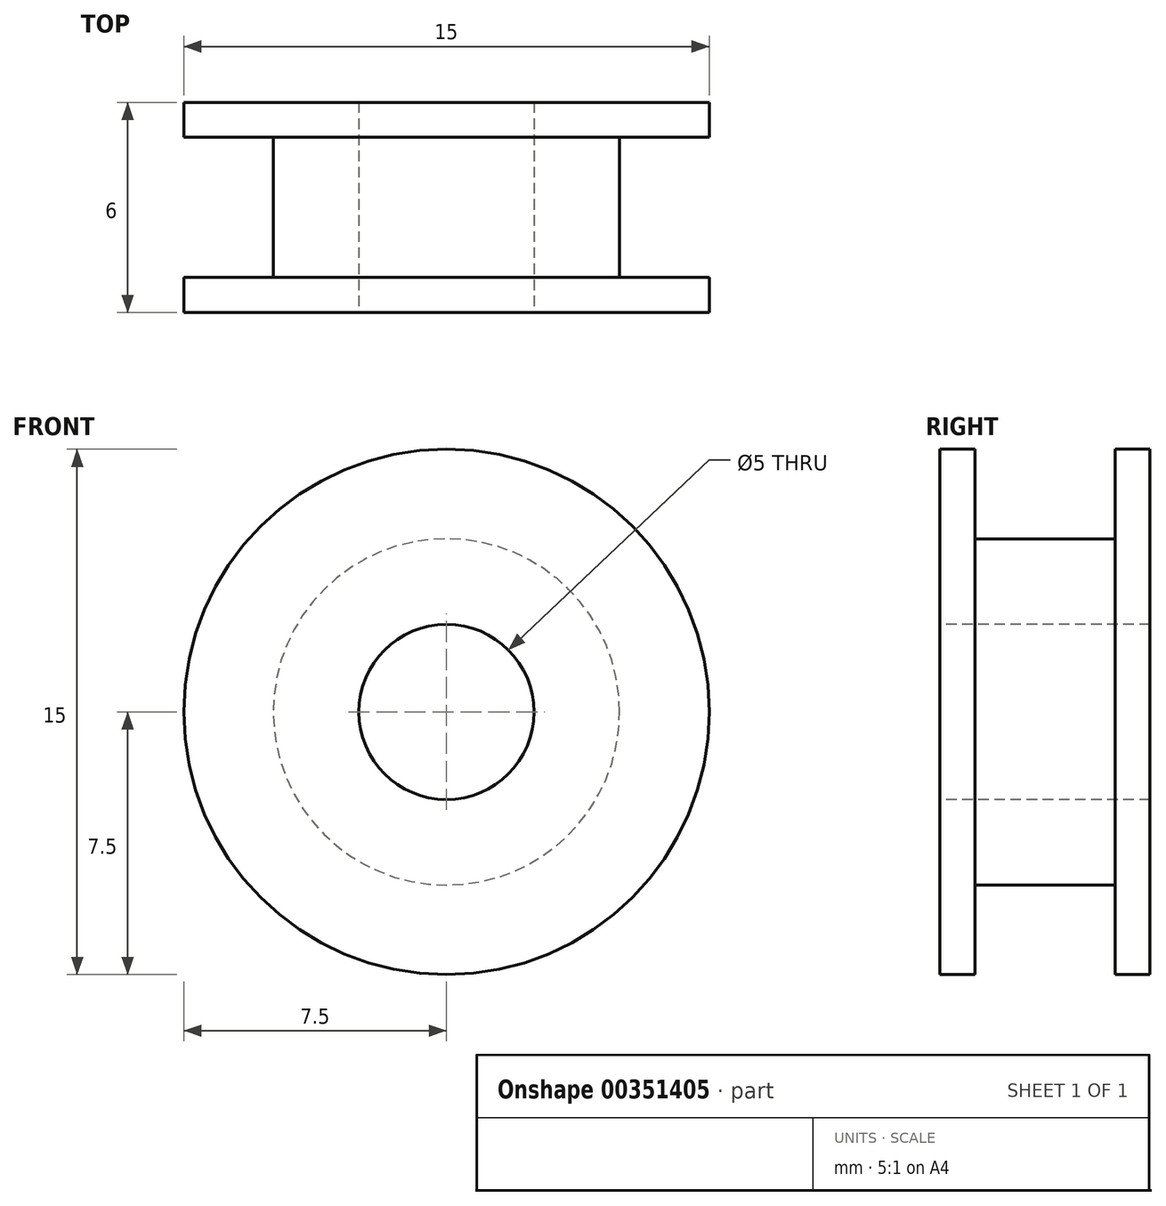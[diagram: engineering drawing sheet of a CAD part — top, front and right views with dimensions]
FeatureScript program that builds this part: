
annotation { "Feature Type Name" : "Feature", "Feature Type Description" : "" }
export const myFeature = defineFeature(function(context is Context, id is Id, definition is map)
    precondition{}
    {
        {
            var Q0;
            Q0=qCreatedBy(makeId("Front.planeOp"),FACE);
            var sketch = newSketch(context, id + "F0", { "sketchPlane" : qUnion([Q0])});
            skCircle(sketch, "E0", {"center": v(0, 0) * mm, "radius": 7.5 * mm});
            skSolve(sketch);
        }
        {
            var Q0;
            Q0 = qSketchRegion(id + "F0", true);
            extrude(context, id + "F1", {"entities" : qUnion([Q0]), "depth" : 1 * mm});
        }
        {
            var Q0;
            Q0=makeQuery(id+"F1.opExtrude","CAP_FACE",FACE,{"disambiguationData":[OSD([sQuery(id+"F0.wireOp",EDGE,"E0")])],"isStart":false});
            var sketch = newSketch(context, id + "F2", { "sketchPlane" : qUnion([Q0])});
            skCircle(sketch, "E1", {"center": v(0, 0) * mm, "radius": 4.94 * mm});
            skSolve(sketch);
        }
        {
            var Q0;
            Q0 = qSketchRegion(id + "F2", true);
            extrude(context, id + "F3", {"entities" : qUnion([Q0]), "operationType" : NewBodyOperationType.ADD, "depth" : 4 * mm});
        }
        {
            var Q0;
            Q0=makeQuery(id+"F3.opExtrude","CAP_FACE",FACE,{"disambiguationData":[OSD([sQuery(id+"F2.wireOp",EDGE,"E1")])],"isStart":false});
            var sketch = newSketch(context, id + "F4", { "sketchPlane" : qUnion([Q0])});
            skCircle(sketch, "E2", {"center": v(0, 0) * mm, "radius": 7.5 * mm});
            skSolve(sketch);
        }
        {
            var Q0;
            Q0 = qSketchRegion(id + "F4", true);
            extrude(context, id + "F5", {"entities" : qUnion([Q0]), "operationType" : NewBodyOperationType.ADD, "depth" : 1 * mm});
        }
        {
            var Q0;
            Q0=makeQuery(id+"F5.opExtrude","CAP_FACE",FACE,{"disambiguationData":[OSD([sQuery(id+"F4.wireOp",EDGE,"E2")])],"isStart":false});
            var sketch = newSketch(context, id + "F6", { "sketchPlane" : qUnion([Q0])});
            skCircle(sketch, "E3", {"center": v(0, 0) * mm, "radius": 2.5 * mm});
            skSolve(sketch);
        }
        {
            var Q0;
            Q0 = qSketchRegion(id + "F6", true);
            extrude(context, id + "F7", {"entities" : qUnion([Q0]), "operationType" : NewBodyOperationType.REMOVE, "oppositeDirection" : true, "depth" : 25 * mm});
        }
    });
